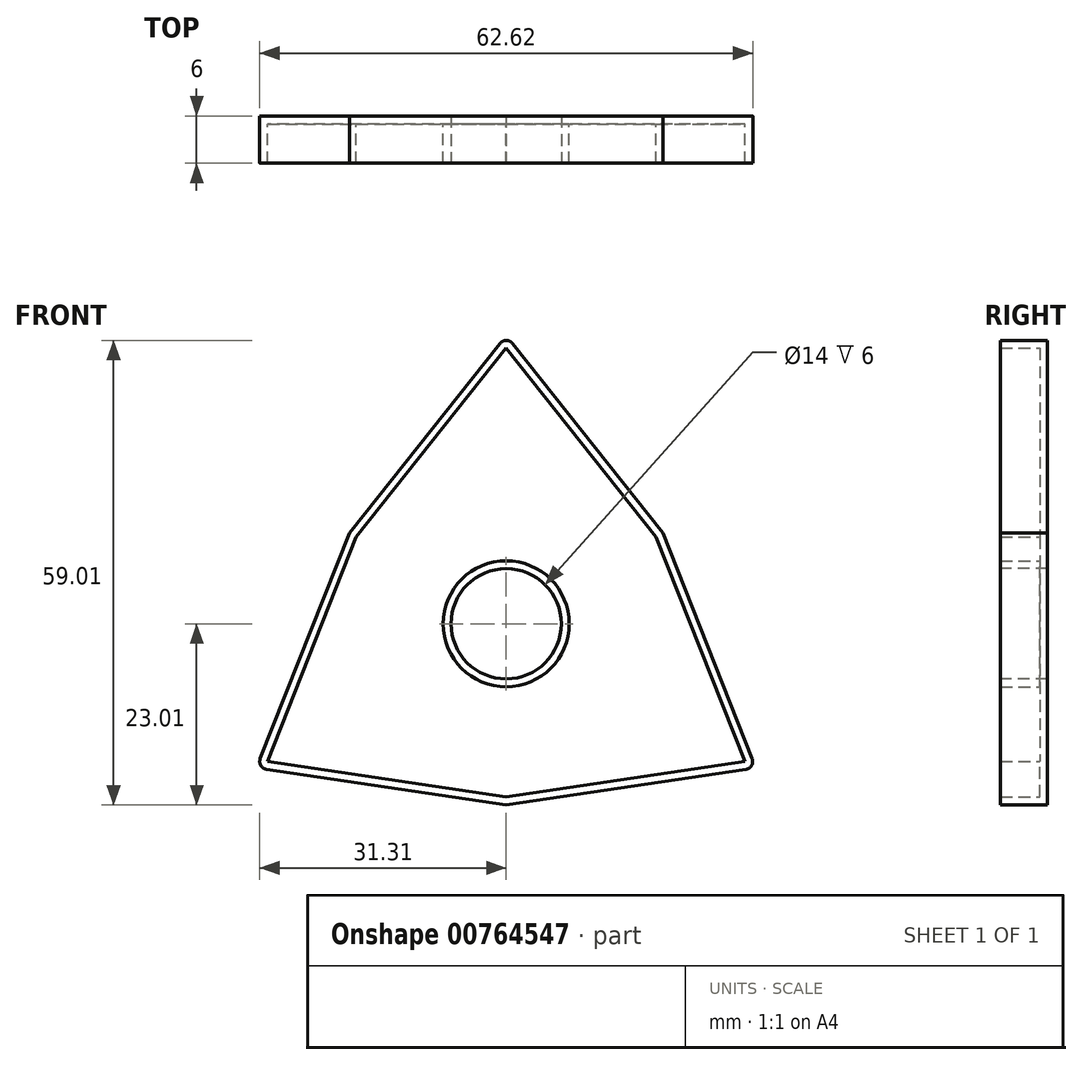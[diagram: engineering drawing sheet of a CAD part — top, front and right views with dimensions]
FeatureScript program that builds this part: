
annotation { "Feature Type Name" : "Feature", "Feature Type Description" : "" }
export const myFeature = defineFeature(function(context is Context, id is Id, definition is map)
    precondition{}
    {
        {
            var Q0;
            Q0=qCreatedBy(makeId("Front.planeOp"),FACE);
            var sketch = newSketch(context, id + "F0", { "sketchPlane" : qUnion([Q0])});
            skLineSegment(sketch, "E0.0", {"start": v(-30.31, -17.5) * mm, "end": v(-19.05, 11) * mm});
            skLineSegment(sketch, "E0.1", {"start": v(-19.05, 11) * mm, "end": v(0, 35) * mm});
            skLineSegment(sketch, "E0.2", {"start": v(0, 35) * mm, "end": v(19.05, 11) * mm});
            skLineSegment(sketch, "E0.3", {"start": v(19.05, 11) * mm, "end": v(30.31, -17.5) * mm});
            skLineSegment(sketch, "E0.4", {"start": v(30.31, -17.5) * mm, "end": v(0, -22) * mm});
            skLineSegment(sketch, "E0.5", {"start": v(0, -22) * mm, "end": v(-30.31, -17.5) * mm});
            skCircle(sketch, "E1", {"center": v(0, 0) * mm, "radius": 8 * mm});
            skLineSegment(sketch, "E2", {"start": v(0, 35) * mm, "end": v(0, 0) * mm, "construction": true});
            skLineSegment(sketch, "E3", {"start": v(0, 0) * mm, "end": v(19.05, 11) * mm, "construction": true});
            skLineSegment(sketch, "E4", {"start": v(30.31, -17.5) * mm, "end": v(0, 0) * mm, "construction": true});
            skLineSegment(sketch, "E5", {"start": v(0, 0) * mm, "end": v(0, -22) * mm, "construction": true});
            skLineSegment(sketch, "E6", {"start": v(-30.31, -17.5) * mm, "end": v(0, 0) * mm, "construction": true});
            skLineSegment(sketch, "E7", {"start": v(0, 0) * mm, "end": v(-19.05, 11) * mm, "construction": true});
            skCircle(sketch, "E8.0", {"center": v(0, 0) * mm, "radius": 7 * mm});
            skLineSegment(sketch, "E9.0", {"start": v(-31.24, -17.13) * mm, "end": v(-19.93, 11.5) * mm});
            skLineSegment(sketch, "E9.1", {"start": v(0.78, 35.62) * mm, "end": v(19.93, 11.5) * mm});
            skLineSegment(sketch, "E9.2", {"start": v(19.93, 11.5) * mm, "end": v(31.24, -17.13) * mm});
            skLineSegment(sketch, "E9.3", {"start": v(-19.93, 11.5) * mm, "end": v(-0.78, 35.62) * mm});
            skLineSegment(sketch, "E9.4", {"start": v(30.46, -18.49) * mm, "end": v(0, -23.01) * mm});
            skLineSegment(sketch, "E9.5", {"start": v(0, -23.01) * mm, "end": v(-30.46, -18.49) * mm});
            skPoint(sketch, "E10.visualSharp", {"position": v(0, 36.6) * mm});
            skArc(sketch, "E10.filletArc", {"start": v(0.78, 35.62) * mm, "mid": v(0, 36) * mm, "end": v(-0.78, 35.62) * mm});
            skPoint(sketch, "E11.visualSharp", {"position": v(31.7, -18.3) * mm});
            skArc(sketch, "E11.filletArc", {"start": v(30.46, -18.49) * mm, "mid": v(31.18, -18) * mm, "end": v(31.24, -17.13) * mm});
            skPoint(sketch, "E12.visualSharp", {"position": v(-31.7, -18.3) * mm});
            skArc(sketch, "E12.filletArc", {"start": v(-31.24, -17.13) * mm, "mid": v(-31.18, -18) * mm, "end": v(-30.46, -18.49) * mm});
            skSolve(sketch);
        }
        {
            var Q0;
            Q0 = qSketchRegion(id + "F0", true);
            var Q1;
            Q1=makeQuery(id+"F0.imprint","IMPRINT",FACE,{"disambiguationData":[TD([[makeQuery(id+"F0.imprint","IMPRINT",EDGE,{"derivedFrom":sQuery(id+"F0.wireOp",EDGE,"E0.0")}),-1.0]])]});
            var Q2;
            Q2=makeQuery(id+"F0.imprint","IMPRINT",FACE,{"disambiguationData":[TD([[makeQuery(id+"F0.imprint","IMPRINT",EDGE,{"derivedFrom":sQuery(id+"F0.wireOp",EDGE,"E1")}),1.0]])]});
            extrude(context, id + "F1", {"entities" : qUnion([Q0, Q1, Q2]), "oppositeDirection" : true, "depth" : 1 * mm, "offsetDistance" : 25 * mm});
        }
        {
            var Q0;
            Q0 = qSketchRegion(id + "F0", true);
            var Q1;
            Q1=makeQuery(id+"F0.imprint","IMPRINT",FACE,{"disambiguationData":[TD([[makeQuery(id+"F0.imprint","IMPRINT",EDGE,{"derivedFrom":sQuery(id+"F0.wireOp",EDGE,"E1")}),1.0]])]});
            extrude(context, id + "F2", {"entities" : qUnion([Q0, Q1]), "operationType" : NewBodyOperationType.ADD, "depth" : 5 * mm, "offsetDistance" : 25 * mm});
        }
    });
